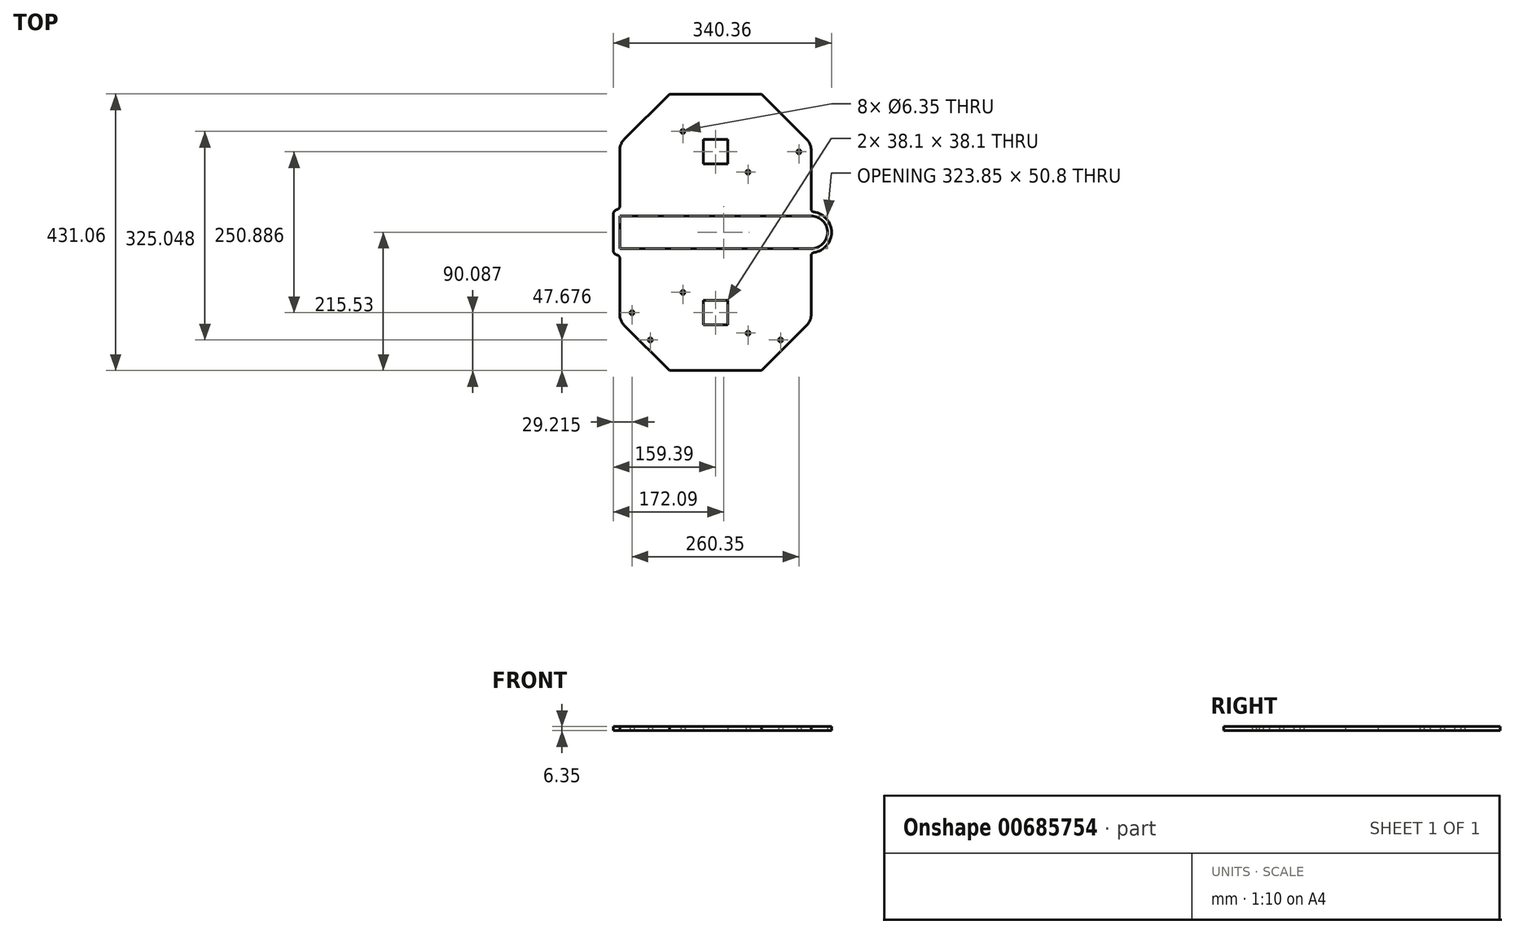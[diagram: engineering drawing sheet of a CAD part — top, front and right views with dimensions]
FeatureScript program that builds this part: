
annotation { "Feature Type Name" : "Feature", "Feature Type Description" : "" }
export const myFeature = defineFeature(function(context is Context, id is Id, definition is map)
    precondition{}
    {
        {
            var Q0;
            Q0=qCreatedBy(makeId("Top.planeOp"),FACE);
            var sketch = newSketch(context, id + "F0", { "sketchPlane" : qUnion([Q0])});
            skPoint(sketch, "E0.middle", {"position": v(0, 0) * mm});
            skLineSegment(sketch, "E1.bottom", {"start": v(-149.22, -25.4) * mm, "end": v(149.23, -25.4) * mm});
            skLineSegment(sketch, "E1.top", {"start": v(-149.23, 25.4) * mm, "end": v(149.23, 25.4) * mm});
            skLineSegment(sketch, "E1.left", {"start": v(-149.22, -25.4) * mm, "end": v(-149.23, 25.4) * mm});
            skLineSegment(sketch, "E2", {"start": v(0, 287.37) * mm, "end": v(-287.37, 0) * mm});
            skLineSegment(sketch, "E3", {"start": v(-287.37, 0) * mm, "end": v(0, -287.37) * mm});
            skLineSegment(sketch, "E4", {"start": v(0, -287.37) * mm, "end": v(287.37, 0) * mm});
            skLineSegment(sketch, "E5", {"start": v(287.37, 0) * mm, "end": v(0, 287.37) * mm});
            skArc(sketch, "E6", {"start": v(149.23, -25.4) * mm, "mid": v(174.63, 0) * mm, "end": v(149.23, 25.4) * mm});
            skPoint(sketch, "E7", {"position": v(-50.17, -63.5) * mm});
            skCircle(sketch, "E8", {"center": v(-50.17, -63.5) * mm, "radius": 3.18 * mm});
            skPoint(sketch, "E9", {"position": v(50.17, -63.5) * mm});
            skCircle(sketch, "E10", {"center": v(50.17, -63.5) * mm, "radius": 3.18 * mm});
            skPoint(sketch, "E11.MirrorP", {"position": v(-50.17, 63.5) * mm});
            skPoint(sketch, "E12.MirrorP", {"position": v(50.17, 63.5) * mm});
            skCircle(sketch, "E13", {"center": v(-50.17, 63.5) * mm, "radius": 3.18 * mm});
            skCircle(sketch, "E14", {"center": v(50.17, 63.5) * mm, "radius": 3.18 * mm});
            skPoint(sketch, "E15", {"position": v(-188.59, 98.78) * mm});
            skPoint(sketch, "E16", {"position": v(188.59, 98.78) * mm});
            skPoint(sketch, "E17.MirrorP", {"position": v(-188.59, -98.78) * mm});
            skPoint(sketch, "E18.MirrorP", {"position": v(188.59, -98.78) * mm});
            skPoint(sketch, "E19", {"position": v(-146.05, 98.78) * mm});
            skPoint(sketch, "E20.MirrorP", {"position": v(146.05, 98.78) * mm});
            skPoint(sketch, "E21.MirrorP", {"position": v(-146.05, -98.78) * mm});
            skPoint(sketch, "E22.MirrorP", {"position": v(146.05, -98.78) * mm});
            skPoint(sketch, "E23", {"position": v(215.53, -71.84) * mm});
            skPoint(sketch, "E24", {"position": v(215.53, 71.84) * mm});
            skPoint(sketch, "E25", {"position": v(-215.53, -71.84) * mm});
            skPoint(sketch, "E26", {"position": v(-215.53, 71.84) * mm});
            skPoint(sketch, "E27", {"position": v(71.84, -215.53) * mm});
            skPoint(sketch, "E28", {"position": v(-71.84, -215.53) * mm});
            skLineSegment(sketch, "E29", {"start": v(-71.84, -215.53) * mm, "end": v(71.84, -215.53) * mm});
            skPoint(sketch, "E30", {"position": v(71.84, 215.53) * mm});
            skPoint(sketch, "E31", {"position": v(-71.84, 215.53) * mm});
            skLineSegment(sketch, "E32", {"start": v(71.84, 215.53) * mm, "end": v(-71.84, 215.53) * mm});
            skLineSegment(sketch, "E33", {"start": v(149.23, -25.4) * mm, "end": v(149.23, -138.14) * mm});
            skLineSegment(sketch, "E34", {"start": v(149.23, 25.4) * mm, "end": v(149.23, 138.14) * mm});
            skLineSegment(sketch, "E35", {"start": v(-149.22, -25.4) * mm, "end": v(-149.22, -138.14) * mm});
            skLineSegment(sketch, "E36", {"start": v(-149.23, 25.4) * mm, "end": v(-149.23, 138.14) * mm});
            skCircle(sketch, "E37", {"center": v(130.18, -125.44) * mm, "radius": 3.18 * mm});
            skLineSegment(sketch, "E38", {"start": v(149.23, 138.14) * mm, "end": v(71.84, 215.53) * mm});
            skPoint(sketch, "E39", {"position": v(149.23, 138.14) * mm});
            skPoint(sketch, "E40", {"position": v(110.53, 176.83) * mm});
            skLineSegment(sketch, "E41", {"start": v(110.53, 176.83) * mm, "end": v(101.55, 167.85) * mm});
            skCircle(sketch, "E42", {"center": v(101.55, 167.85) * mm, "radius": 3.18 * mm});
            skPoint(sketch, "E43", {"position": v(-110.53, 176.83) * mm});
            skLineSegment(sketch, "E44", {"start": v(-110.53, 176.83) * mm, "end": v(-101.55, 167.85) * mm});
            skCircle(sketch, "E45", {"center": v(-101.55, 167.85) * mm, "radius": 3.18 * mm});
            skCircle(sketch, "E46.MirrorC", {"center": v(101.55, -167.85) * mm, "radius": 3.18 * mm});
            skCircle(sketch, "E47.MirrorC", {"center": v(-101.55, -167.85) * mm, "radius": 3.18 * mm});
            skPoint(sketch, "E48", {"position": v(149.23, -35.56) * mm});
            skArc(sketch, "E49.0", {"start": v(149.23, -31.75) * mm, "mid": v(180.97, 0) * mm, "end": v(149.23, 31.75) * mm});
            skLineSegment(sketch, "E50", {"start": v(-149.23, 35.56) * mm, "end": v(-159.38, 35.56) * mm});
            skLineSegment(sketch, "E51", {"start": v(-159.38, 35.56) * mm, "end": v(-159.38, -35.56) * mm});
            skLineSegment(sketch, "E52", {"start": v(-159.38, -35.56) * mm, "end": v(-149.22, -35.56) * mm});
            skCircle(sketch, "E53.MirrorC", {"center": v(130.18, 125.44) * mm, "radius": 3.18 * mm});
            skCircle(sketch, "E54.MirrorC", {"center": v(-130.18, 125.44) * mm, "radius": 3.18 * mm});
            skCircle(sketch, "E55.MirrorC", {"center": v(-130.18, -125.44) * mm, "radius": 3.18 * mm});
            skLineSegment(sketch, "E56", {"start": v(0, 125.44) * mm, "end": v(0, 106.4) * mm});
            skLineSegment(sketch, "E57", {"start": v(-19.05, 106.4) * mm, "end": v(19.05, 106.4) * mm});
            skLineSegment(sketch, "E58", {"start": v(-19.05, 106.4) * mm, "end": v(-19.05, 144.5) * mm});
            skLineSegment(sketch, "E59", {"start": v(-19.05, 144.5) * mm, "end": v(19.05, 144.5) * mm});
            skLineSegment(sketch, "E60", {"start": v(19.05, 144.5) * mm, "end": v(19.05, 106.4) * mm});
            skLineSegment(sketch, "E61", {"start": v(0, 125.44) * mm, "end": v(9.88, 125.44) * mm});
            skPoint(sketch, "E62", {"position": v(50.8, 157.2) * mm});
            skCircle(sketch, "E63", {"center": v(50.8, 157.2) * mm, "radius": 3.18 * mm});
            skCircle(sketch, "E64.MirrorC", {"center": v(-50.8, 157.2) * mm, "radius": 3.18 * mm});
            skCircle(sketch, "E65.MirrorC", {"center": v(50.8, 93.7) * mm, "radius": 3.18 * mm});
            skCircle(sketch, "E66.MirrorC", {"center": v(-50.8, 93.7) * mm, "radius": 3.18 * mm});
            skLineSegment(sketch, "E67.MirrorCS", {"start": v(-19.05, -144.5) * mm, "end": v(19.05, -144.5) * mm});
            skLineSegment(sketch, "E68.MirrorCS", {"start": v(19.05, -144.5) * mm, "end": v(19.05, -106.4) * mm});
            skLineSegment(sketch, "E69.MirrorCS", {"start": v(-19.05, -106.4) * mm, "end": v(-19.05, -144.5) * mm});
            skLineSegment(sketch, "E70.MirrorCS", {"start": v(-19.05, -106.4) * mm, "end": v(19.05, -106.4) * mm});
            skPoint(sketch, "E71.MirrorP", {"position": v(50.8, -157.2) * mm});
            skCircle(sketch, "E72.MirrorC", {"center": v(50.8, -93.7) * mm, "radius": 3.18 * mm});
            skCircle(sketch, "E73.MirrorC", {"center": v(50.8, -157.2) * mm, "radius": 3.18 * mm});
            skCircle(sketch, "E74.MirrorC", {"center": v(-50.8, -157.2) * mm, "radius": 3.18 * mm});
            skCircle(sketch, "E75.MirrorC", {"center": v(-50.8, -93.7) * mm, "radius": 3.18 * mm});
            skSolve(sketch);
        }
        {
            var Q0;
            {var subQ0=sQuery(id+"F0.wireOp",EDGE,"E6");Q0=makeQuery(id+"F0.imprint","IMPRINT",FACE,{"disambiguationData":[TD([[makeQuery(id+"F0.imprint","IMPRINT",EDGE,{"derivedFrom":subQ0}),-1.0]])]});}
            var Q1;
            {var subQ2=sQuery(id+"F0.wireOp",EDGE,"E1.left");Q1=makeQuery(id+"F0.imprint","IMPRINT",FACE,{"disambiguationData":[TD([[makeQuery(id+"F0.imprint","IMPRINT",EDGE,{"derivedFrom":subQ2}),1.0]])]});}
            var Q2;
            Q2=makeQuery(id+"F0.imprint","IMPRINT",FACE,{"disambiguationData":[TD([[makeQuery(id+"F0.imprint","IMPRINT",EDGE,{"derivedFrom":sQuery(id+"F0.wireOp",EDGE,"E55.MirrorC")}),-1.0]])]});
            var Q3;
            Q3=makeQuery(id+"F0.imprint","IMPRINT",FACE,{"disambiguationData":[TD([[makeQuery(id+"F0.imprint","IMPRINT",EDGE,{"derivedFrom":sQuery(id+"F0.wireOp",EDGE,"E47.MirrorC")}),-1.0]])]});
            var Q4;
            Q4=makeQuery(id+"F0.imprint","IMPRINT",FACE,{"disambiguationData":[TD([[makeQuery(id+"F0.imprint","IMPRINT",EDGE,{"derivedFrom":sQuery(id+"F0.wireOp",EDGE,"E8")}),1.0]])]});
            var Q5;
            Q5=makeQuery(id+"F0.imprint","IMPRINT",FACE,{"disambiguationData":[TD([[makeQuery(id+"F0.imprint","IMPRINT",EDGE,{"derivedFrom":sQuery(id+"F0.wireOp",EDGE,"E75.MirrorC")}),-1.0]])]});
            var Q6;
            {var subQ1=sQuery(id+"F0.wireOp",EDGE,"E1.bottom");Q6=makeQuery(id+"F0.imprint","IMPRINT",FACE,{"disambiguationData":[TD([[makeQuery(id+"F0.imprint","IMPRINT",EDGE,{"derivedFrom":subQ1}),-1.0]])]});}
            var Q7;
            Q7=makeQuery(id+"F0.imprint","IMPRINT",FACE,{"disambiguationData":[TD([[makeQuery(id+"F0.imprint","IMPRINT",EDGE,{"derivedFrom":sQuery(id+"F0.wireOp",EDGE,"E74.MirrorC")}),1.0]])]});
            var Q8;
            Q8=makeQuery(id+"F0.imprint","IMPRINT",FACE,{"disambiguationData":[TD([[makeQuery(id+"F0.imprint","IMPRINT",EDGE,{"derivedFrom":sQuery(id+"F0.wireOp",EDGE,"E10")}),1.0]])]});
            var Q9;
            Q9=makeQuery(id+"F0.imprint","IMPRINT",FACE,{"disambiguationData":[TD([[makeQuery(id+"F0.imprint","IMPRINT",EDGE,{"derivedFrom":sQuery(id+"F0.wireOp",EDGE,"E72.MirrorC")}),1.0]])]});
            var Q10;
            Q10=makeQuery(id+"F0.imprint","IMPRINT",FACE,{"disambiguationData":[TD([[makeQuery(id+"F0.imprint","IMPRINT",EDGE,{"derivedFrom":sQuery(id+"F0.wireOp",EDGE,"E73.MirrorC")}),-1.0]])]});
            var Q11;
            Q11=makeQuery(id+"F0.imprint","IMPRINT",FACE,{"disambiguationData":[TD([[makeQuery(id+"F0.imprint","IMPRINT",EDGE,{"derivedFrom":sQuery(id+"F0.wireOp",EDGE,"E46.MirrorC")}),-1.0]])]});
            var Q12;
            Q12=makeQuery(id+"F0.imprint","IMPRINT",FACE,{"disambiguationData":[TD([[makeQuery(id+"F0.imprint","IMPRINT",EDGE,{"derivedFrom":sQuery(id+"F0.wireOp",EDGE,"E37")}),1.0]])]});
            var Q13;
            Q13=makeQuery(id+"F0.imprint","IMPRINT",FACE,{"disambiguationData":[TD([[makeQuery(id+"F0.imprint","IMPRINT",EDGE,{"derivedFrom":sQuery(id+"F0.wireOp",EDGE,"E54.MirrorC")}),1.0]])]});
            var Q14;
            Q14=makeQuery(id+"F0.imprint","IMPRINT",FACE,{"disambiguationData":[TD([[makeQuery(id+"F0.imprint","IMPRINT",EDGE,{"derivedFrom":sQuery(id+"F0.wireOp",EDGE,"E66.MirrorC")}),1.0]])]});
            var Q15;
            Q15=makeQuery(id+"F0.imprint","IMPRINT",FACE,{"disambiguationData":[TD([[makeQuery(id+"F0.imprint","IMPRINT",EDGE,{"derivedFrom":sQuery(id+"F0.wireOp",EDGE,"E13")}),1.0]])]});
            var Q16;
            Q16=makeQuery(id+"F0.imprint","IMPRINT",FACE,{"disambiguationData":[TD([[makeQuery(id+"F0.imprint","IMPRINT",EDGE,{"derivedFrom":sQuery(id+"F0.wireOp",EDGE,"E14")}),1.0]])]});
            var Q17;
            Q17=makeQuery(id+"F0.imprint","IMPRINT",FACE,{"disambiguationData":[TD([[makeQuery(id+"F0.imprint","IMPRINT",EDGE,{"derivedFrom":sQuery(id+"F0.wireOp",EDGE,"E65.MirrorC")}),-1.0]])]});
            var Q18;
            Q18=makeQuery(id+"F0.imprint","IMPRINT",FACE,{"disambiguationData":[TD([[makeQuery(id+"F0.imprint","IMPRINT",EDGE,{"derivedFrom":sQuery(id+"F0.wireOp",EDGE,"E63")}),1.0]])]});
            var Q19;
            {var subQ15=sQuery(id+"F0.wireOp",EDGE,"E1.top");Q19=makeQuery(id+"F0.imprint","IMPRINT",FACE,{"disambiguationData":[TD([[makeQuery(id+"F0.imprint","IMPRINT",EDGE,{"derivedFrom":subQ15}),1.0]])]});}
            var Q20;
            Q20=makeQuery(id+"F0.imprint","IMPRINT",FACE,{"disambiguationData":[TD([[makeQuery(id+"F0.imprint","IMPRINT",EDGE,{"derivedFrom":sQuery(id+"F0.wireOp",EDGE,"E64.MirrorC")}),-1.0]])]});
            var Q21;
            Q21=makeQuery(id+"F0.imprint","IMPRINT",FACE,{"disambiguationData":[TD([[makeQuery(id+"F0.imprint","IMPRINT",EDGE,{"derivedFrom":sQuery(id+"F0.wireOp",EDGE,"E45")}),1.0]])]});
            var Q22;
            Q22=makeQuery(id+"F0.imprint","IMPRINT",FACE,{"disambiguationData":[TD([[makeQuery(id+"F0.imprint","IMPRINT",EDGE,{"derivedFrom":sQuery(id+"F0.wireOp",EDGE,"E42")}),1.0]])]});
            var Q23;
            Q23=makeQuery(id+"F0.imprint","IMPRINT",FACE,{"disambiguationData":[TD([[makeQuery(id+"F0.imprint","IMPRINT",EDGE,{"derivedFrom":sQuery(id+"F0.wireOp",EDGE,"E53.MirrorC")}),-1.0]])]});
            extrude(context, id + "F1", {"entities" : qUnion([Q0, Q1, Q2, Q3, Q4, Q5, Q6, Q7, Q8, Q9, Q10, Q11, Q12, Q13, Q14, Q15, Q16, Q17, Q18, Q19, Q20, Q21, Q22, Q23]), "depth" : 6.35 * mm});
        }
        {
            var Q0;
            Q0=makeQuery(id+"F1.opExtrude","SWEPT_EDGE",EDGE,{"disambiguationData":[OSD([sQuery(id+"F0.wireOp",EDGE,"E4"),sQuery(id+"F0.wireOp",EDGE,"E33")])]});
            var Q1;
            Q1=makeQuery(id+"F1.opExtrude","SWEPT_EDGE",EDGE,{"disambiguationData":[OSD([sQuery(id+"F0.wireOp",EDGE,"E3"),sQuery(id+"F0.wireOp",EDGE,"E35")])]});
            var Q2;
            Q2=makeQuery(id+"F1.opExtrude","SWEPT_EDGE",EDGE,{"disambiguationData":[OSD([sQuery(id+"F0.wireOp",EDGE,"E5"),sQuery(id+"F0.wireOp",EDGE,"E34")])]});
            var Q3;
            Q3=makeQuery(id+"F1.opExtrude","SWEPT_EDGE",EDGE,{"disambiguationData":[OSD([sQuery(id+"F0.wireOp",EDGE,"E2"),sQuery(id+"F0.wireOp",EDGE,"E36")])]});
            fillet(context, id + "F2", {"entities" : qUnion([Q0, Q1, Q2, Q3]), "radius" : 25.4 * mm, "tangentPropagation" : true, "allowEdgeOverflow" : false});
        }
        {
            var Q0;
            Q0=makeQuery(id+"F1.opExtrude","SWEPT_EDGE",EDGE,{"disambiguationData":[OSD([sQuery(id+"F0.wireOp",EDGE,"E33"),sQuery(id+"F0.wireOp",EDGE,"E49.0")])]});
            var Q1;
            Q1=makeQuery(id+"F1.opExtrude","SWEPT_EDGE",EDGE,{"disambiguationData":[OSD([sQuery(id+"F0.wireOp",EDGE,"E34"),sQuery(id+"F0.wireOp",EDGE,"E49.0")])]});
            fillet(context, id + "F3", {"entities" : qUnion([Q0, Q1]), "radius" : 5.08 * mm, "tangentPropagation" : true, "allowEdgeOverflow" : false});
        }
        {
            var Q0;
            Q0=makeQuery(id+"F1.opExtrude","SWEPT_EDGE",EDGE,{"disambiguationData":[OSD([sQuery(id+"F0.wireOp",EDGE,"E51"),sQuery(id+"F0.wireOp",EDGE,"E52")])]});
            var Q1;
            Q1=makeQuery(id+"F1.opExtrude","SWEPT_EDGE",EDGE,{"disambiguationData":[OSD([sQuery(id+"F0.wireOp",EDGE,"E50"),sQuery(id+"F0.wireOp",EDGE,"E51")])]});
            fillet(context, id + "F4", {"entities" : qUnion([Q0, Q1]), "radius" : 7.62 * mm, "tangentPropagation" : true, "allowEdgeOverflow" : false});
        }
        {
            var Q0;
            Q0=makeQuery(id+"F1.opExtrude","SWEPT_EDGE",EDGE,{"disambiguationData":[OSD([sQuery(id+"F0.wireOp",EDGE,"E35"),sQuery(id+"F0.wireOp",EDGE,"E52")])]});
            var Q1;
            Q1=makeQuery(id+"F1.opExtrude","SWEPT_EDGE",EDGE,{"disambiguationData":[OSD([sQuery(id+"F0.wireOp",EDGE,"E36"),sQuery(id+"F0.wireOp",EDGE,"E50")])]});
            fillet(context, id + "F5", {"entities" : qUnion([Q0, Q1]), "radius" : 5.08 * mm, "tangentPropagation" : true, "allowEdgeOverflow" : false});
        }
    });
